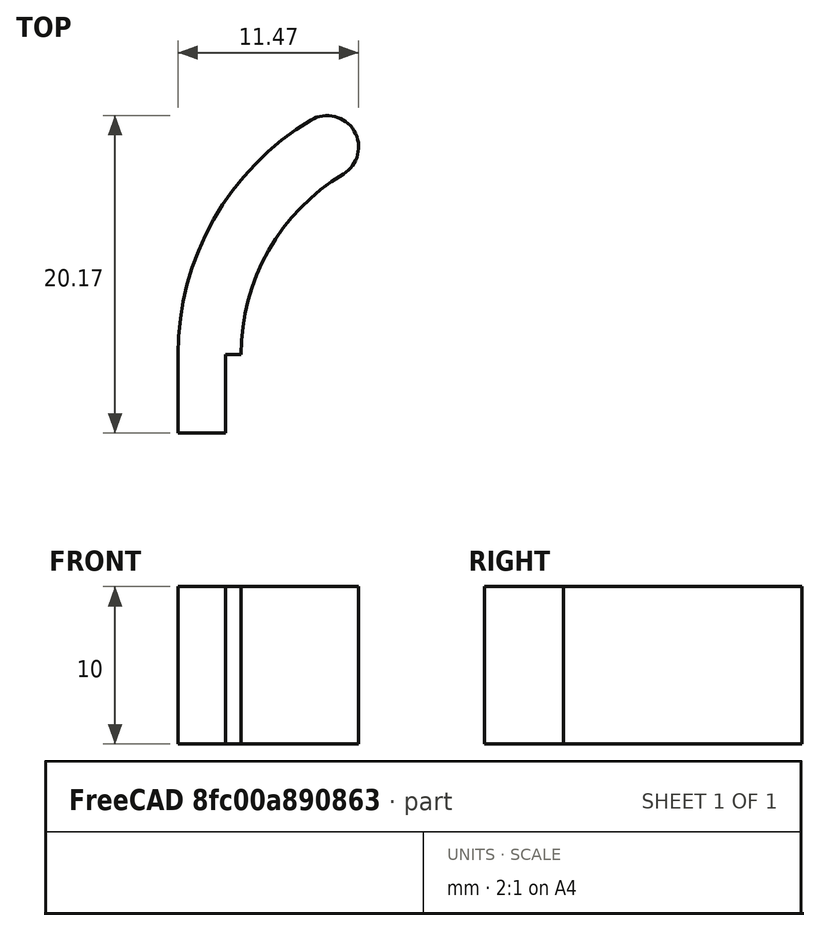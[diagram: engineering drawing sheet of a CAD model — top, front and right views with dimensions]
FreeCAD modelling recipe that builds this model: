
FCSTD DOCUMENT  (FreeCAD 0.14R3702 (Git))
Label: solapas-base
License: CC-BY 3.0
LicenseURL: http://creativecommons.org/licenses/by/3.0/
objects: Sketcher::SketchObject×1, Part::Extrusion×1
note: 2 computed .brp shape members not serialized (recipe doc carries the construction recipe); baked Part::Feature solids carry a one-line shape summary decoded from their .brp

FEATURE [Sketcher::SketchObject] Sketch  label="main"
  sketch-geometry (8):
    g0: LineSegment StartX=-3.69647 StartY=-10.6721 StartZ=0 EndX=-0.696471 EndY=-10.6721 EndZ=0
    g1: LineSegment StartX=-0.696471 StartY=-10.6721 StartZ=0 EndX=-0.696471 EndY=-5.67212 EndZ=0
    g2: LineSegment StartX=-3.69647 StartY=-5.67212 StartZ=0 EndX=-3.69647 EndY=-10.6721 EndZ=0
    g3: LineSegment [constr] StartX=-18.5483 StartY=-5.67212 StartZ=0 EndX=48.2943 EndY=-5.67212 EndZ=0
    g4: ArcOfCircle CenterX=13.6545 CenterY=-5.67212 CenterZ=0 NormalX=0 NormalY=0 NormalZ=1 Radius=17.351 StartAngle=2.11033 EndAngle=3.14159
    g5: ArcOfCircle CenterX=13.6545 CenterY=-5.67212 CenterZ=0 NormalX=0 NormalY=0 NormalZ=1 Radius=13.351 StartAngle=2.11033 EndAngle=3.14159
    g6: ArcOfCircle CenterX=5.7682 CenterY=7.49825 CenterZ=0 NormalX=0 NormalY=0 NormalZ=1 Radius=2 StartAngle=5.25192 EndAngle=8.39351
    g7: LineSegment StartX=-0.696471 StartY=-5.67212 StartZ=0 EndX=0.303529 EndY=-5.67212 EndZ=0
  constraints (21):
    c: Horizontal(g3)
    c: PointOnObject(g2,g3)
    c: Horizontal(g0)
    c: Vertical(g2)
    c: Vertical(g1)
    c: DistanceX(g0) = 3
    c: DistanceY(g2) = -5
    c: Coincident(g2,g4)
    c: Coincident(g4,g5)
    c: Tangent(g4,g2)
    c: Tangent(g6,g4)
    c: Tangent(g5,g6)
    c: Horizontal(g7)
    c: Coincident(g1,g7)
    c: Coincident(g5,g7)
    c: DistanceX(g7) = 1
    c: Coincident(g0,g1)
    c: Coincident(g0,g2)
    c: Coincident(g4,g6)
    c: Coincident(g5,g6)
    c: PointOnObject(g5,g3)
FEATURE [Part::Extrusion] Extrude
  Base = -> Sketch
  Dir = (0,0,10)
  Solid = true
